# Revit family: X651UHD
name_source: partatom
category: Communication Devices
revit_build: Autodesk Revit Architecture 2012 (Build: 20110309_2315(x64)
units: mm (PartAtom-declared; Revit-internal decimal feet)

## types (1)
- X651UHD
    Assembly Code = E1020500
    CONNECTIVITY- Input Terminals- Audio = Audio MIni-Jack, DispkayPort Audio, HDMI Audio x4
    CONNECTIVITY- Input Terminals- Digital = DisplayPort (w/ HDCP), HDMI x4 (w/ HDCP), DVI-D (Dual-Link with HDCP)
    CONNECTIVITY- Input Terminals- External Control = RS232C, LAN, IR Remote In
    CONNECTIVITY- Output Terminals- Audio = Audio Mini-Jack
    CONNECTIVITY- Output Terminals- External Control = LAN
    CONNECTIVITY- Output Terminals- Speakers = External Speaker Terminal (10W x 2)
    CONNECTIVITY- USB hub = USB Upstream / USB Downstream, USB Service Port
    Cost = 0 $
    Cost MSRP = 0 $
    Cost Project = 0 $
    Description = UHD Professional Large Format Displays
    Frame Width = 0' - 0 3/4"
    LCD MODULE- Active Screen Area (WxH) = 56.2 x 31.6in : 1428.5 x 803.5mm
    LCD MODULE- Aspect Ratio = 16:9
    LCD MODULE- Brightness (Typical/Max) = 320 / 450 cd/m2
    LCD MODULE- Contrast Ratio (Typical) = 1300:1
    LCD MODULE- Displayable Colors = Greater than 1.07 Billion
    LCD MODULE- Native Resolution = 3840 x 2160 at 60Hz
    LCD MODULE- Orientation = Landscape / Portrait
    LCD MODULE- Panel Technology = S-IPS with Edge LED Backlighting
    LCD MODULE- Viewable Image Size = 65in
    LCD MODULE- Viewing Angle = 178deg Vert, 178deg Hor 989U / 89D / 89L / 89R) @ CR>10
    Manufacturer = NEC Display Solutions
    Model = X651UHD
    Overall Depth = 0' - 3 1/2"
    Overall Height = 2' - 9 1/4"
    Overall Width = 4' - 9 3/4"
    PHYSICAL SPECS- Bezel Width (L/R, T/B) = 0.7in/0.7in; 0.7in/0.7in : 17.5mm/17.5mm; 17.5mm / 17.5mm
    PHYSICAL SPECS- Net Dimensions (no stand, WxHxD) = 57.8 x 33.2 x 3.4in / 1468.4 x 843.6 x 87.4mm
    PHYSICAL SPECS- Net Weight (no stand) = 92.6lbs / 42.0kg
    PHYSICAL SPECS- VESA Hole Config = 400x400mm (4-hole)
    POWER CONSUMPTION- Auto Power Save = <6.0W
    POWER CONSUMPTION- Auto Standby = <0.5W
    POWER CONSUMPTION- Current Rating = 3.6A @100-120V, 1.4A @220-240A
    POWER CONSUMPTION- On (Typical) = 150W
    URL = www.necdisplay.com
    Version = 1.1

## geometry (parser evidence)
native form markers: Sweep x1
no freeform markers — native parametric forms only
